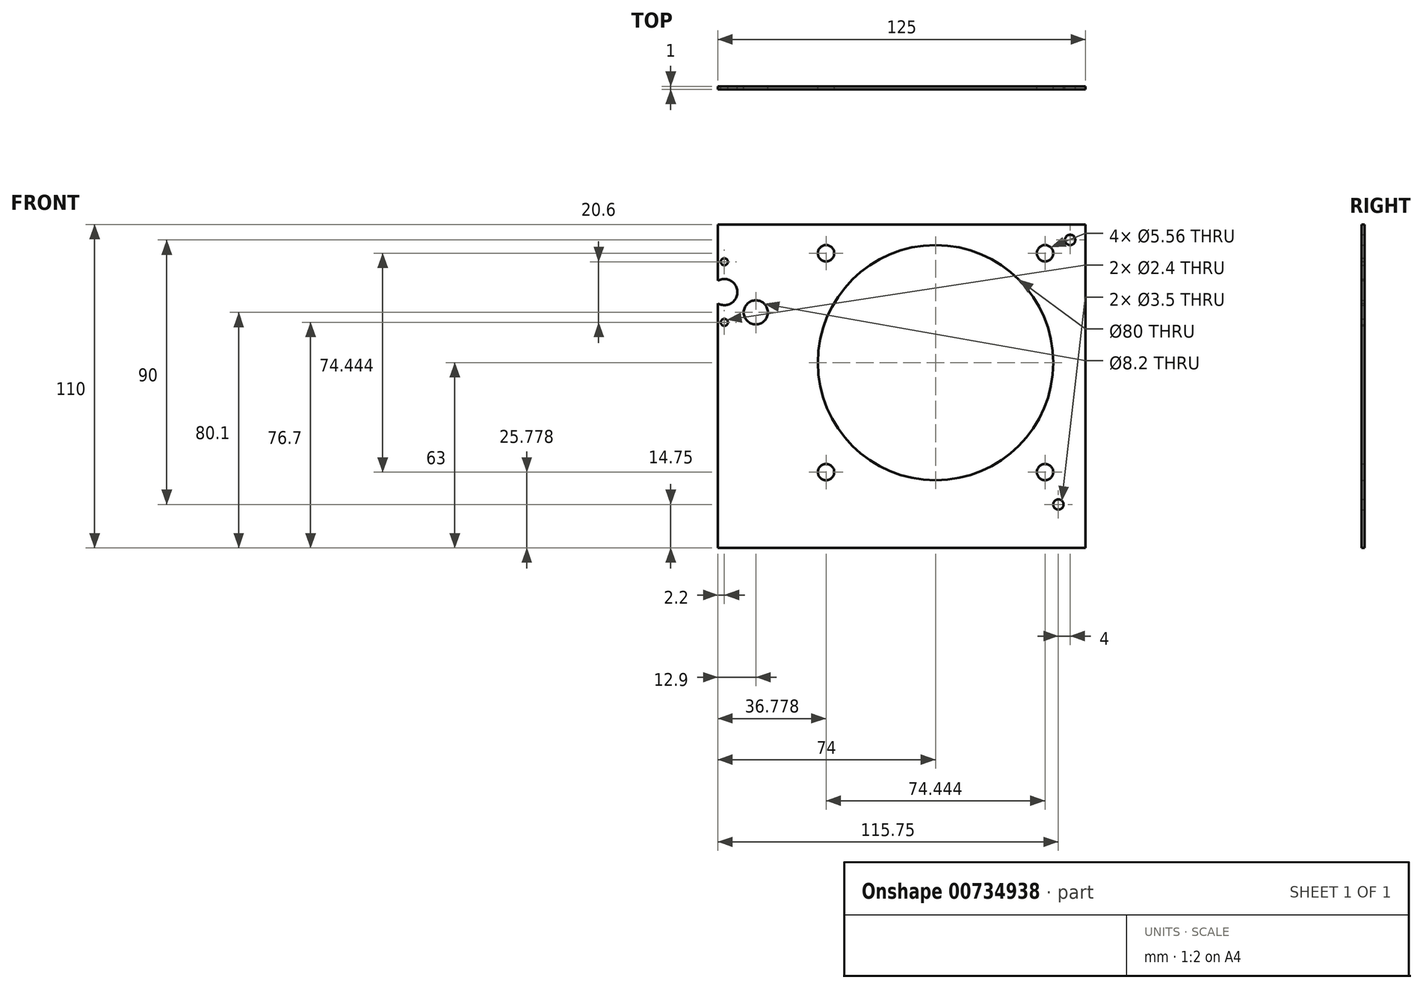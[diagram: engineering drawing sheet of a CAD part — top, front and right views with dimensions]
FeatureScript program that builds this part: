
annotation { "Feature Type Name" : "Feature", "Feature Type Description" : "" }
export const myFeature = defineFeature(function(context is Context, id is Id, definition is map)
    precondition{}
    {
        {
            var Q0;
            Q0=qCreatedBy(makeId("Front.planeOp"),FACE);
            var sketch = newSketch(context, id + "F0", { "sketchPlane" : qUnion([Q0])});
            skLineSegment(sketch, "E0.bottom", {"start": v(-62.5, -55) * mm, "end": v(62.5, -55) * mm});
            skLineSegment(sketch, "E0.top", {"start": v(-62.5, 55) * mm, "end": v(62.5, 55) * mm});
            skLineSegment(sketch, "E0.left", {"start": v(-62.5, -55) * mm, "end": v(-62.5, 55) * mm});
            skLineSegment(sketch, "E0.right", {"start": v(62.5, -55) * mm, "end": v(62.5, 55) * mm});
            skPoint(sketch, "E0.middle", {"position": v(0, 0) * mm});
            skLineSegment(sketch, "E1.bottom", {"start": v(-104.5, 44) * mm, "end": v(-90.5, 44) * mm, "construction": true});
            skLineSegment(sketch, "E1.top", {"start": v(-104.5, 14) * mm, "end": v(-90.5, 14) * mm, "construction": true});
            skLineSegment(sketch, "E1.left", {"start": v(-104.5, 44) * mm, "end": v(-104.5, 14) * mm, "construction": true});
            skLineSegment(sketch, "E1.right", {"start": v(-90.5, 44) * mm, "end": v(-90.5, 14) * mm, "construction": true});
            skLineSegment(sketch, "E2.bottom", {"start": v(-75.5, 43) * mm, "end": v(-45.5, 43) * mm, "construction": true});
            skLineSegment(sketch, "E2.top", {"start": v(-75.5, 21) * mm, "end": v(-45.5, 21) * mm, "construction": true});
            skLineSegment(sketch, "E2.left", {"start": v(-75.5, 43) * mm, "end": v(-75.5, 21) * mm, "construction": true});
            skLineSegment(sketch, "E2.right", {"start": v(-45.5, 43) * mm, "end": v(-45.5, 21) * mm, "construction": true});
            skCircle(sketch, "E3", {"center": v(-102.25, -40.25) * mm, "radius": 1.75 * mm});
            skCircle(sketch, "E4", {"center": v(57.25, 49.75) * mm, "radius": 1.75 * mm});
            skCircle(sketch, "E5", {"center": v(-66.25, 49.75) * mm, "radius": 1.75 * mm});
            skCircle(sketch, "E6", {"center": v(53.25, -40.25) * mm, "radius": 1.75 * mm});
            skLineSegment(sketch, "E7.bottom", {"start": v(51.5, -32) * mm, "end": v(-28.5, -32) * mm, "construction": true});
            skLineSegment(sketch, "E7.top", {"start": v(51.5, 48) * mm, "end": v(-28.5, 48) * mm, "construction": true});
            skLineSegment(sketch, "E7.left", {"start": v(51.5, -32) * mm, "end": v(51.5, 48) * mm, "construction": true});
            skLineSegment(sketch, "E7.right", {"start": v(-28.5, -32) * mm, "end": v(-28.5, 48) * mm, "construction": true});
            skCircle(sketch, "E8", {"center": v(11.5, 8) * mm, "radius": 40 * mm});
            skPoint(sketch, "E8.first.point", {"position": v(11.5, 48) * mm});
            skPoint(sketch, "E8.second.point", {"position": v(51.5, 8) * mm});
            skPoint(sketch, "E8.third.point", {"position": v(11.5, -32) * mm});
            skLineSegment(sketch, "E9.bottom", {"start": v(-28.5, 48) * mm, "end": v(-22.94, 48) * mm, "construction": true});
            skLineSegment(sketch, "E9.top", {"start": v(-28.5, 42.44) * mm, "end": v(-22.94, 42.44) * mm, "construction": true});
            skLineSegment(sketch, "E9.left", {"start": v(-28.5, 48) * mm, "end": v(-28.5, 42.44) * mm, "construction": true});
            skLineSegment(sketch, "E9.right", {"start": v(-22.94, 48) * mm, "end": v(-22.94, 42.44) * mm, "construction": true});
            skCircle(sketch, "E10", {"center": v(-25.72, 45.22) * mm, "radius": 2.78 * mm});
            skPoint(sketch, "E10.first.point", {"position": v(-25.72, 48) * mm});
            skPoint(sketch, "E10.second.point", {"position": v(-22.94, 45.22) * mm});
            skPoint(sketch, "E10.third.point", {"position": v(-25.72, 42.44) * mm});
            skLineSegment(sketch, "E11.bottom", {"start": v(51.5, 48) * mm, "end": v(45.94, 48) * mm, "construction": true});
            skLineSegment(sketch, "E11.top", {"start": v(51.5, 42.44) * mm, "end": v(45.94, 42.44) * mm, "construction": true});
            skLineSegment(sketch, "E11.left", {"start": v(51.5, 48) * mm, "end": v(51.5, 42.44) * mm, "construction": true});
            skLineSegment(sketch, "E11.right", {"start": v(45.94, 48) * mm, "end": v(45.94, 42.44) * mm, "construction": true});
            skLineSegment(sketch, "E12.bottom", {"start": v(51.5, -32) * mm, "end": v(45.94, -32) * mm, "construction": true});
            skLineSegment(sketch, "E12.top", {"start": v(51.5, -26.44) * mm, "end": v(45.94, -26.44) * mm, "construction": true});
            skLineSegment(sketch, "E12.left", {"start": v(51.5, -32) * mm, "end": v(51.5, -26.44) * mm, "construction": true});
            skLineSegment(sketch, "E12.right", {"start": v(45.94, -32) * mm, "end": v(45.94, -26.44) * mm, "construction": true});
            skLineSegment(sketch, "E13.bottom", {"start": v(-28.5, -32) * mm, "end": v(-22.94, -32) * mm, "construction": true});
            skLineSegment(sketch, "E13.top", {"start": v(-28.5, -26.44) * mm, "end": v(-22.94, -26.44) * mm, "construction": true});
            skLineSegment(sketch, "E13.left", {"start": v(-28.5, -32) * mm, "end": v(-28.5, -26.44) * mm, "construction": true});
            skLineSegment(sketch, "E13.right", {"start": v(-22.94, -32) * mm, "end": v(-22.94, -26.44) * mm, "construction": true});
            skCircle(sketch, "E14", {"center": v(48.72, 45.22) * mm, "radius": 2.78 * mm});
            skPoint(sketch, "E14.first.point", {"position": v(48.72, 48) * mm});
            skPoint(sketch, "E14.second.point", {"position": v(45.94, 45.22) * mm});
            skPoint(sketch, "E14.third.point", {"position": v(48.72, 42.44) * mm});
            skCircle(sketch, "E15", {"center": v(48.72, -29.22) * mm, "radius": 2.78 * mm});
            skPoint(sketch, "E15.first.point", {"position": v(48.72, -26.44) * mm});
            skPoint(sketch, "E15.second.point", {"position": v(45.94, -29.22) * mm});
            skPoint(sketch, "E15.third.point", {"position": v(48.72, -32) * mm});
            skCircle(sketch, "E16", {"center": v(-25.72, -29.22) * mm, "radius": 2.78 * mm});
            skPoint(sketch, "E16.first.point", {"position": v(-25.72, -26.44) * mm});
            skPoint(sketch, "E16.second.point", {"position": v(-28.5, -29.22) * mm});
            skPoint(sketch, "E16.third.point", {"position": v(-25.72, -32) * mm});
            skCircle(sketch, "E17", {"center": v(-60.3, 32) * mm, "radius": 4.45 * mm});
            skLineSegment(sketch, "E18", {"start": v(-60.3, 21.7) * mm, "end": v(-60.3, 42.3) * mm, "construction": true});
            skCircle(sketch, "E19", {"center": v(-60.3, 42.3) * mm, "radius": 1.2 * mm});
            skCircle(sketch, "E20", {"center": v(-60.3, 21.7) * mm, "radius": 1.2 * mm});
            skPoint(sketch, "E21", {"position": v(-75.5, 32) * mm});
            skPoint(sketch, "E22", {"position": v(-60.5, 21) * mm});
            skPoint(sketch, "E23", {"position": v(-49.6, 25.1) * mm});
            skCircle(sketch, "E24", {"center": v(-49.6, 25.1) * mm, "radius": 4.1 * mm});
            skPoint(sketch, "E25", {"position": v(-45.5, 32) * mm});
            skLineSegment(sketch, "E26", {"start": v(-61.5, 55) * mm, "end": v(-61.5, -55) * mm, "construction": true});
            skSolve(sketch);
        }
        {
            var Q0;
            {var subQ0=sQuery(id+"F0.wireOp",EDGE,"cfSl68OW-Y9iN-8OMg-qRQz-4nlVoakqv04e");var subQ1=sQuery(id+"F0.wireOp",EDGE,"vP8uru67-1rKL-aZWj-Ed0x-q8X2hZfk60Cs.left");var subQ2=makeQuery(id+"F0.imprint","INTERSECT",VERTEX,{"derivedFrom":[subQ1,subQ0]});Q0=makeQuery(id+"F0.imprint","IMPRINT",FACE,{"disambiguationData":[TD([[makeQuery(id+"F0.imprint","IMPRINT",EDGE,{"disambiguationData":[TD([[subQ2,1.0]])],"derivedFrom":subQ1}),-1.0]])]});}
            var Q1;
            {var subQ0=sQuery(id+"F0.wireOp",EDGE,"cfSl68OW-Y9iN-8OMg-qRQz-4nlVoakqv04e");var subQ1=sQuery(id+"F0.wireOp",EDGE,"vP8uru67-1rKL-aZWj-Ed0x-q8X2hZfk60Cs.bottom");var subQ2=makeQuery(id+"F0.imprint","INTERSECT",VERTEX,{"derivedFrom":[subQ1,subQ0]});Q1=makeQuery(id+"F0.imprint","IMPRINT",FACE,{"disambiguationData":[TD([[makeQuery(id+"F0.imprint","IMPRINT",EDGE,{"disambiguationData":[TD([[subQ2,1.0]])],"derivedFrom":subQ1}),1.0]])]});}
            var Q2;
            {var subQ0=sQuery(id+"F0.wireOp",EDGE,"PTcjDCUc-MgrD-nLkz-FqYk-Pj8Vo6t2aX3y");var subQ1=sQuery(id+"F0.wireOp",EDGE,"vP8uru67-1rKL-aZWj-Ed0x-q8X2hZfk60Cs.left");var subQ2=makeQuery(id+"F0.imprint","INTERSECT",VERTEX,{"derivedFrom":[subQ1,subQ0]});Q2=makeQuery(id+"F0.imprint","IMPRINT",FACE,{"disambiguationData":[TD([[makeQuery(id+"F0.imprint","IMPRINT",EDGE,{"disambiguationData":[TD([[subQ2,-1.0]])],"derivedFrom":subQ1}),-1.0]])]});}
            var Q3;
            {var subQ0=sQuery(id+"F0.wireOp",EDGE,"PTcjDCUc-MgrD-nLkz-FqYk-Pj8Vo6t2aX3y");var subQ1=sQuery(id+"F0.wireOp",EDGE,"vP8uru67-1rKL-aZWj-Ed0x-q8X2hZfk60Cs.top");var subQ2=makeQuery(id+"F0.imprint","INTERSECT",VERTEX,{"derivedFrom":[subQ1,subQ0]});Q3=makeQuery(id+"F0.imprint","IMPRINT",FACE,{"disambiguationData":[TD([[makeQuery(id+"F0.imprint","IMPRINT",EDGE,{"disambiguationData":[TD([[subQ2,1.0]])],"derivedFrom":subQ1}),-1.0]])]});}
            var Q4;
            {var subQ0=sQuery(id+"F0.wireOp",EDGE,"e6uunRbi-GojN-M6QF-zxjB-Brp06QCMidCW");var subQ1=sQuery(id+"F0.wireOp",EDGE,"af8417be-5bd7-453a-83a2-fc172ac16551.2");var subQ2=makeQuery(id+"F0.imprint","INTERSECT",VERTEX,{"derivedFrom":[subQ1,subQ0]});Q4=makeQuery(id+"F0.imprint","IMPRINT",FACE,{"disambiguationData":[TD([[makeQuery(id+"F0.imprint","IMPRINT",EDGE,{"disambiguationData":[TD([[subQ2,-1.0]])],"derivedFrom":subQ1}),-1.0]])]});}
            var Q5;
            {var subQ0=sQuery(id+"F0.wireOp",EDGE,"Twv16H5i-imJu-2RaP-C3eQ-dalo2saDfy5s");var subQ1=sQuery(id+"F0.wireOp",EDGE,"vP8uru67-1rKL-aZWj-Ed0x-q8X2hZfk60Cs.right");var subQ2=makeQuery(id+"F0.imprint","INTERSECT",VERTEX,{"derivedFrom":[subQ1,subQ0]});Q5=makeQuery(id+"F0.imprint","IMPRINT",FACE,{"disambiguationData":[TD([[makeQuery(id+"F0.imprint","IMPRINT",EDGE,{"disambiguationData":[TD([[subQ2,1.0]])],"derivedFrom":subQ1}),1.0]])]});}
            var Q6;
            {var subQ0=sQuery(id+"F0.wireOp",EDGE,"PTcjDCUc-MgrD-nLkz-FqYk-Pj8Vo6t2aX3y");var subQ1=sQuery(id+"F0.wireOp",EDGE,"af8417be-5bd7-453a-83a2-fc172ac16551.1");var subQ2=makeQuery(id+"F0.imprint","INTERSECT",VERTEX,{"derivedFrom":[subQ1,subQ0]});Q6=makeQuery(id+"F0.imprint","IMPRINT",FACE,{"disambiguationData":[TD([[makeQuery(id+"F0.imprint","IMPRINT",EDGE,{"disambiguationData":[TD([[subQ2,-1.0]])],"derivedFrom":subQ1}),-1.0]])]});}
            var Q7;
            {var subQ0=sQuery(id+"F0.wireOp",EDGE,"e6uunRbi-GojN-M6QF-zxjB-Brp06QCMidCW");var subQ1=sQuery(id+"F0.wireOp",EDGE,"vP8uru67-1rKL-aZWj-Ed0x-q8X2hZfk60Cs.top");var subQ2=makeQuery(id+"F0.imprint","INTERSECT",VERTEX,{"derivedFrom":[subQ1,subQ0]});Q7=makeQuery(id+"F0.imprint","IMPRINT",FACE,{"disambiguationData":[TD([[makeQuery(id+"F0.imprint","IMPRINT",EDGE,{"disambiguationData":[TD([[subQ2,-1.0]])],"derivedFrom":subQ1}),-1.0]])]});}
            var Q8;
            {var subQ0=sQuery(id+"F0.wireOp",EDGE,"Twv16H5i-imJu-2RaP-C3eQ-dalo2saDfy5s");var subQ1=sQuery(id+"F0.wireOp",EDGE,"af8417be-5bd7-453a-83a2-fc172ac16551.0");var subQ2=makeQuery(id+"F0.imprint","INTERSECT",VERTEX,{"derivedFrom":[subQ1,subQ0]});Q8=makeQuery(id+"F0.imprint","IMPRINT",FACE,{"disambiguationData":[TD([[makeQuery(id+"F0.imprint","IMPRINT",EDGE,{"disambiguationData":[TD([[subQ2,-1.0]])],"derivedFrom":subQ1}),1.0]])]});}
            var Q9;
            {var subQ0=sQuery(id+"F0.wireOp",EDGE,"Twv16H5i-imJu-2RaP-C3eQ-dalo2saDfy5s");var subQ1=sQuery(id+"F0.wireOp",EDGE,"vP8uru67-1rKL-aZWj-Ed0x-q8X2hZfk60Cs.bottom");var subQ2=makeQuery(id+"F0.imprint","INTERSECT",VERTEX,{"derivedFrom":[subQ1,subQ0]});Q9=makeQuery(id+"F0.imprint","IMPRINT",FACE,{"disambiguationData":[TD([[makeQuery(id+"F0.imprint","IMPRINT",EDGE,{"disambiguationData":[TD([[subQ2,-1.0]])],"derivedFrom":subQ1}),1.0]])]});}
            var Q10;
            {var subQ0=sQuery(id+"F0.wireOp",EDGE,"e6uunRbi-GojN-M6QF-zxjB-Brp06QCMidCW");var subQ1=sQuery(id+"F0.wireOp",EDGE,"vP8uru67-1rKL-aZWj-Ed0x-q8X2hZfk60Cs.right");var subQ2=makeQuery(id+"F0.imprint","INTERSECT",VERTEX,{"derivedFrom":[subQ1,subQ0]});Q10=makeQuery(id+"F0.imprint","IMPRINT",FACE,{"disambiguationData":[TD([[makeQuery(id+"F0.imprint","IMPRINT",EDGE,{"disambiguationData":[TD([[subQ2,-1.0]])],"derivedFrom":subQ1}),1.0]])]});}
            var Q11;
            {var subQ0=sQuery(id+"F0.wireOp",EDGE,"45dMGhS0-YLeI-dV8t-4P02-Nx6Z4lcdnOo9");var subQ1=sQuery(id+"F0.wireOp",EDGE,"af8417be-5bd7-453a-83a2-fc172ac16551.0");var subQ2=makeQuery(id+"F0.imprint","INTERSECT",VERTEX,{"derivedFrom":[subQ1,subQ0]});Q11=makeQuery(id+"F0.imprint","IMPRINT",FACE,{"disambiguationData":[TD([[makeQuery(id+"F0.imprint","IMPRINT",EDGE,{"disambiguationData":[TD([[subQ2,-1.0]])],"derivedFrom":subQ1}),1.0]])]});}
            var Q12;
            Q12=makeQuery(id+"F0.imprint","IMPRINT",FACE,{"disambiguationData":[TD([[makeQuery(id+"F0.imprint","IMPRINT",EDGE,{"derivedFrom":sQuery(id+"F0.wireOp",EDGE,"E0.bottom")}),1.0]])]});
            var Q13;
            {var subQ0=sQuery(id+"F0.wireOp",EDGE,"vP8uru67-1rKL-aZWj-Ed0x-q8X2hZfk60Cs.right");var subQ1=sQuery(id+"F0.wireOp",EDGE,"vP8uru67-1rKL-aZWj-Ed0x-q8X2hZfk60Cs.top");var subQ2=makeQuery(id+"F0.imprint","INTERSECT",VERTEX,{"derivedFrom":[subQ1,subQ0]});Q13=makeQuery(id+"F0.imprint","IMPRINT",FACE,{"disambiguationData":[TD([[makeQuery(id+"F0.imprint","IMPRINT",EDGE,{"disambiguationData":[TD([[subQ2,1.0]])],"derivedFrom":subQ1}),-1.0]])]});}
            var Q14;
            {var subQ0=sQuery(id+"F0.wireOp",EDGE,"vP8uru67-1rKL-aZWj-Ed0x-q8X2hZfk60Cs.left");var subQ1=sQuery(id+"F0.wireOp",EDGE,"vP8uru67-1rKL-aZWj-Ed0x-q8X2hZfk60Cs.bottom");var subQ2=makeQuery(id+"F0.imprint","INTERSECT",VERTEX,{"derivedFrom":[subQ1,subQ0]});Q14=makeQuery(id+"F0.imprint","IMPRINT",FACE,{"disambiguationData":[TD([[makeQuery(id+"F0.imprint","IMPRINT",EDGE,{"disambiguationData":[TD([[subQ2,-1.0]])],"derivedFrom":subQ1}),1.0]])]});}
            var Q15;
            {var subQ0=sQuery(id+"F0.wireOp",EDGE,"vP8uru67-1rKL-aZWj-Ed0x-q8X2hZfk60Cs.right");var subQ1=sQuery(id+"F0.wireOp",EDGE,"vP8uru67-1rKL-aZWj-Ed0x-q8X2hZfk60Cs.bottom");var subQ2=makeQuery(id+"F0.imprint","INTERSECT",VERTEX,{"derivedFrom":[subQ1,subQ0]});Q15=makeQuery(id+"F0.imprint","IMPRINT",FACE,{"disambiguationData":[TD([[makeQuery(id+"F0.imprint","IMPRINT",EDGE,{"disambiguationData":[TD([[subQ2,1.0]])],"derivedFrom":subQ1}),1.0]])]});}
            var Q16;
            {var subQ0=sQuery(id+"F0.wireOp",EDGE,"vP8uru67-1rKL-aZWj-Ed0x-q8X2hZfk60Cs.left");var subQ1=sQuery(id+"F0.wireOp",EDGE,"vP8uru67-1rKL-aZWj-Ed0x-q8X2hZfk60Cs.top");var subQ2=makeQuery(id+"F0.imprint","INTERSECT",VERTEX,{"derivedFrom":[subQ1,subQ0]});Q16=makeQuery(id+"F0.imprint","IMPRINT",FACE,{"disambiguationData":[TD([[makeQuery(id+"F0.imprint","IMPRINT",EDGE,{"disambiguationData":[TD([[subQ2,-1.0]])],"derivedFrom":subQ1}),-1.0]])]});}
            var Q17;
            Q17=makeQuery(id+"F0.imprint","IMPRINT",FACE,{"disambiguationData":[TD([[makeQuery(id+"F0.imprint","IMPRINT",EDGE,{"derivedFrom":sQuery(id+"F0.wireOp",EDGE,"E1.bottom")}),-1.0]])]});
            var Q18;
            Q18=makeQuery(id+"F0.imprint","IMPRINT",FACE,{"disambiguationData":[TD([[makeQuery(id+"F0.imprint","IMPRINT",EDGE,{"derivedFrom":sQuery(id+"F0.wireOp",EDGE,"E2.bottom")}),-1.0]])]});
            extrude(context, id + "F1", {"entities" : qUnion([Q0, Q1, Q2, Q3, Q4, Q5, Q6, Q7, Q8, Q9, Q10, Q11, Q12, Q13, Q14, Q15, Q16, Q17, Q18]), "depth" : 1 * mm, "offsetDistance" : 25 * mm});
        }
    });
